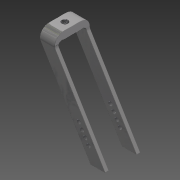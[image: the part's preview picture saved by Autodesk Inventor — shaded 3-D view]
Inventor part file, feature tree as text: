
AUTODESK INVENTOR PART (.ipt)
format: ipt  version: 2015 (Build 190159000, 159)  size: 663,552 bytes
history: native  units: mm
features: sketch x8, other x5, fillet x3, hole x2, sweep x1, loft x1, mirror x1, pattern_linear x1, projected_geometry x1
ambient origin geometry x8: Origin, YZ Plane, XZ Plane, XY Plane, X Axis, Y Axis, Z Axis, Center Point
bodies: Body1 (feature_tree)
feature tree (23):
  other  "Bryła1"
  sweep  "Przeciągnięcie1"
  other  "Płaszczyzna konstrukcyjna1"
  sketch  "Szkic3"
  sketch  "Szkic4"
  other  "Płaszczyzna konstrukcyjna2"
  sketch  "Szkic5"
  other  "Płaszczyzna konstrukcyjna3"
  loft  "Wyciągnięcie złożone1"
  mirror  "Odbicie lustrzane2"
  other  "Płaszczyzna konstrukcyjna4"
  hole  "Otwór1"  [1 undecoded]
  hole  "Otwór2"  [1 undecoded]
  pattern_linear  "Szyk prostokątny2"  Spacing1=0.0mm  [1 undecoded]
  fillet  "Zaokrąglenie4"  Radius=12.0mm
  fillet  "Zaokrąglenie5"  Radius=22.5mm
  fillet  "Zaokrąglenie6"  Radius=15.0mm
  sketch  "Szkic1"
  sketch  "Szkic2"
  projected_geometry  "Pętla rzutowana1"
  sketch  "Szkic6"
  sketch  "Szkic7"
  sketch  "Szkic8"
note: 3 required parameter values undecoded (feature->parameter linkage not recoverable at this tier; creation-order binding heuristic only, values carry confidence <= 0.55)
